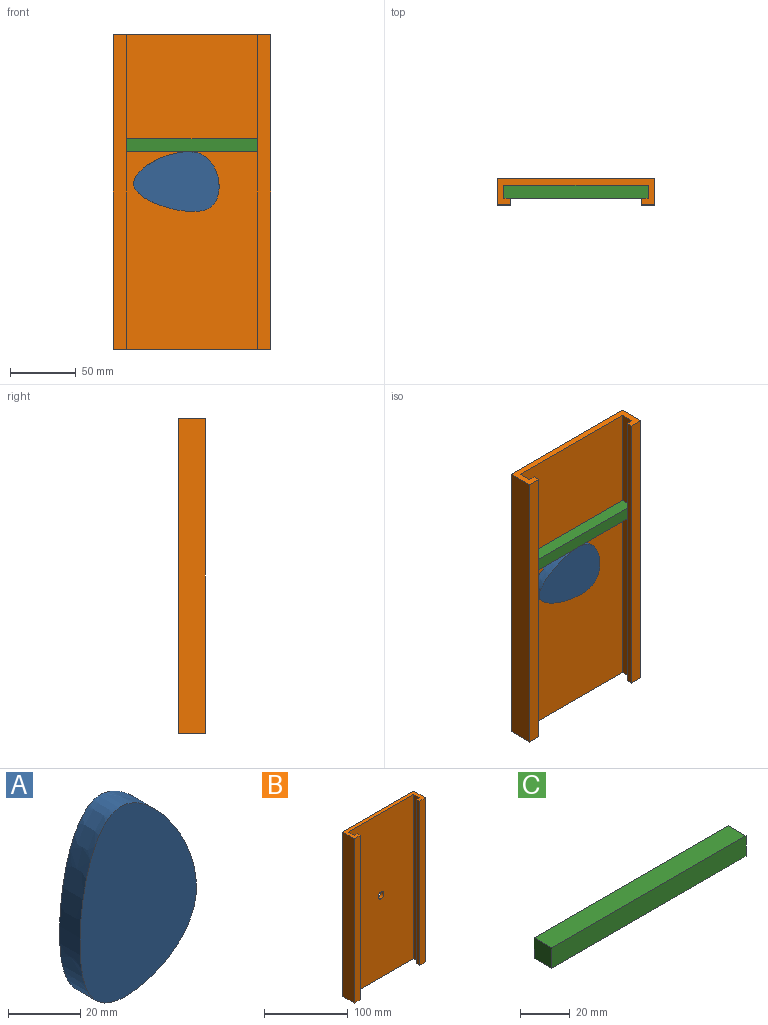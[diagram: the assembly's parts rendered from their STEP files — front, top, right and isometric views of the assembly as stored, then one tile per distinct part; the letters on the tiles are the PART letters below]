
ASSEMBLY  parts=3 mates=2
PART A: 5 faces, bbox 51x15x69 mm
  f0: plane 10x10mm, normal (0,1,0), area 78.5mm2, adj f1
  f1: cylinder r=5mm len=10mm, axis (0,-1,0), area 219.9mm2, adj f0,f4
  f2: extruded ~65.1x45.46mm, area 1405.8mm2, adj f3,f4
  f3: plane 69.02x51.05mm, normal (0,-1,0), area 2271.9mm2, adj f2
  f4: plane 69.02x51.05mm, normal (0,1,0), area 2193.4mm2, adj f1,f2
PART B: 15 faces, bbox 120x20x240 mm
  f0: plane 240x5mm, normal (1,0,0), area 1200mm2, adj f1,f3,f8,f13
  f1: plane 120x20mm, normal (0,0,-1), area 800mm2, adj f0,f2,f4,f5,f6,f7,f8,f9
  f2: plane 240x5mm, normal (-1,0,0), area 1200mm2, adj f1,f3,f6,f11
  f3: plane 120x20mm, normal (0,0,1), area 800mm2, adj f0,f2,f4,f5,f6,f7,f8,f9
  f4: plane 240x110mm, normal (0,-1,0), area 26321.5mm2, adj f1,f3,f5,f7,f14
  f5: plane 240x10mm, normal (-1,0,0), area 2400mm2, adj f1,f3,f4,f6
  f6: plane 240x5mm, normal (0,1,0), area 1200mm2, adj f1,f2,f3,f5
  f7: plane 240x10mm, normal (1,0,0), area 2400mm2, adj f1,f3,f4,f8
  f8: plane 240x5mm, normal (0,1,0), area 1200mm2, adj f0,f1,f3,f7
  f9: plane 240x120mm, normal (0,1,0), area 28721.5mm2, adj f1,f3,f10,f12,f14
  f10: plane 240x20mm, normal (1,0,0), area 4800mm2, adj f1,f3,f9,f11
  f11: plane 240x10mm, normal (0,-1,0), area 2400mm2, adj f1,f2,f3,f10
  f12: plane 240x20mm, normal (-1,0,0), area 4800mm2, adj f1,f3,f9,f13
  f13: plane 240x10mm, normal (0,-1,0), area 2400mm2, adj f0,f1,f3,f12
  f14: cylinder r=5mm len=10mm, axis (0,-1,0), area 157.1mm2, adj f4,f9
PART C: 6 faces, bbox 110x10x10 mm
  f0: plane 10x10mm, normal (1,0,0), area 100mm2, adj f1,f2,f4,f5
  f1: plane 110x10mm, normal (0,0,1), area 1100mm2, adj f0,f3,f4,f5
  f2: plane 110x10mm, normal (0,0,-1), area 1100mm2, adj f0,f3,f4,f5
  f3: plane 10x10mm, normal (-1,0,0), area 100mm2, adj f1,f2,f4,f5
  f4: plane 110x10mm, normal (0,1,0), area 1100mm2, adj f0,f1,f2,f3
  f5: plane 110x10mm, normal (0,-1,0), area 1100mm2, adj f0,f1,f2,f3
PLACE A rot(axis=(0,-1,0),80.9deg) t=(-19.01,0,-118.49)mm
PLACE B at identity fixed
PLACE C t=(0,0,-79.31)mm
MATE revolute B.f14 <-> A.f1  axis (0,1,0) through (0,7,0)mm
MATE slider B.f3 <-> C.f1  axis (0,0,1) through (-55,2,120)mm
